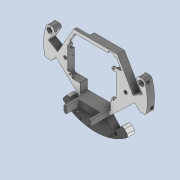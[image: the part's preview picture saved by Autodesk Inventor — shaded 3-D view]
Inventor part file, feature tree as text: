
AUTODESK INVENTOR PART (.ipt)
format: ipt  version: 2020.4 (Build 244396000, 396)  size: 959,488 bytes
history: native  units: mm
features: extrude x28, sketch x28, projected_geometry x14, plane x8, fillet x2
ambient origin geometry x8: Origin, YZ Plane, XZ Plane, XY Plane, X Axis, Y Axis, Z Axis, Center Point
bodies: Solid1 (feature_tree)
feature tree (80):
  extrude  "Extrusion1"  TaperAngle=0.0deg  [1 undecoded]
  extrude  "Extrusion2"  Depth=85.8mm
  extrude  "Extrusion3"  TaperAngle=60.0deg  [1 undecoded]
  extrude  "Extrusion4"  Depth=4.22mm
  extrude  "Extrusion5"  Depth=4.22mm
  extrude  "Extrusion6"  Depth=78.0mm
  extrude  "Extrusion7"  Depth=12.0mm
  extrude  "Extrusion8"  Depth=4.22mm
  fillet  "Fillet1"  Radius=4.22mm
  extrude  "Extrusion9"  Depth=65.0mm
  extrude  "Extrusion10"  TaperAngle=30.0deg  [1 undecoded]
  extrude  "Extrusion11"  TaperAngle=105.0deg  [1 undecoded]
  extrude  "Extrusion12"  Depth=3.0mm
  extrude  "Extrusion13"  Depth=3.0mm
  extrude  "Extrusion14"  Depth=3.0mm
  extrude  "Extrusion15"  Depth=44.0mm
  extrude  "Extrusion16"  Depth=72.0mm
  extrude  "Extrusion17"  Depth=30.0mm
  plane  "Work Plane1"
  extrude  "Extrusion18"  Depth=20.0mm
  plane  "Work Plane2"
  extrude  "Extrusion19"  Depth=3.0mm
  plane  "Work Plane3"
  extrude  "Extrusion20"  Depth=50.0mm
  plane  "Work Plane4"
  extrude  "Extrusion21"  Depth=75.0mm
  plane  "Work Plane5"
  extrude  "Extrusion22"  Depth=25.0mm
  plane  "Work Plane6"
  extrude  "Extrusion23"  Depth=10.0mm
  fillet  "Fillet3"  Radius=10.0mm
  extrude  "Extrusion30"  Depth=5.5mm
  extrude  "Extrusion31"  Depth=5.5mm
  extrude  "Extrusion32"  Depth=3.11mm
  plane  "Work Plane10"
  extrude  "Extrusion33"  Depth=3.11mm
  plane  "Work Plane11"
  extrude  "Extrusion34"  Depth=10.0mm TaperAngle=0.0deg
  sketch  "Sketch1"  dims[d0=171.6mm d1=3.0mm d2=3.0mm d3=3.0mm d4=76.0mm d5=22.0mm d6=73.0mm d7=33.2mm d8=72.0mm d9=32.0mm d10=29.0mm d11=30.0deg d12=150.0deg d13=45.0deg d14=135.0deg d15=18.0mm d16=66.0mm d17=62.0mm d18=60.0mm d19=5.0mm d20=62.240108mm d21=18.0mm d22=66.0mm d23=25.833623mm d24=52.933108mm d25=43.5mm d26=20.0mm d27=66.5mm d28=18.0mm d29=18.0mm d30=0.0mm d31=0.0mm]
  sketch  "Sketch3"  dims[d32=12.0mm d33=0.0mm d34=85.8mm]
  sketch  "Sketch4"  dims[d35=60.0deg d36=60.0deg]
  sketch  "Sketch5"  dims[d37=4.22mm d38=4.22mm]
  sketch  "Sketch6"  dims[d39=4.22mm d40=4.22mm]
  sketch  "Sketch7"  dims[d41=9.55mm d42=0.0mm d43=78.0mm]
  sketch  "Sketch8"  dims[d44=78.0mm d45=12.0mm]
  sketch  "Sketch9"  dims[d46=12.0mm d47=4.22mm d48=4.22mm]
  projected_geometry  "Projected Loop1"
  sketch  "Sketch10"  dims[d49=8.0mm d50=0.0mm d51=65.0mm]
  sketch  "Sketch11"  dims[d52=75.0deg d53=30.0deg]
  sketch  "Sketch12"  dims[d54=75.0deg d55=105.0deg]
  projected_geometry  "Projected Loop2"
  sketch  "Sketch13"  dims[d56=3.0mm d57=3.0mm]
  projected_geometry  "Projected Loop3"
  sketch  "Sketch14"  dims[d58=3.0mm d59=3.0mm]
  projected_geometry  "Projected Loop4"
  sketch  "Sketch16"  dims[d60=3.0mm d61=3.0mm]
  projected_geometry  "Projected Loop5"
  sketch  "Sketch17"  dims[d62=44.0mm d63=44.0mm]
  projected_geometry  "Projected Loop6"
  sketch  "Sketch18"  dims[d64=72.0mm d65=72.0mm]
  projected_geometry  "Projected Loop7"
  sketch  "Sketch19"  dims[d66=20.0mm d67=30.0mm]
  projected_geometry  "Projected Loop8"
  sketch  "Sketch20"  dims[d68=30.0mm d69=20.0mm]
  sketch  "Sketch21"  dims[d70=3.0mm d71=3.0mm]
  sketch  "Sketch22"  dims[d72=50.0mm d73=50.0mm]
  projected_geometry  "Projected Loop9"
  sketch  "Sketch23"  dims[d74=75.0mm d75=75.0mm]
  projected_geometry  "Projected Loop10"
  sketch  "Sketch24"  dims[d76=25.0mm d77=25.0mm]
  projected_geometry  "Projected Loop11"
  sketch  "Sketch25"  dims[d78=79.0mm d79=79.0mm d80=10.0mm d81=0.0mm]
  projected_geometry  "Projected Loop12"
  sketch  "Sketch32"  dims[d82=5.5mm d83=5.5mm]
  sketch  "Sketch33"  dims[d84=5.5mm d85=5.5mm]
  projected_geometry  "Projected Loop16"
  sketch  "Sketch34"  dims[d86=2.0mm d87=0.0mm d88=3.11mm]
  projected_geometry  "Projected Loop17"
  sketch  "Sketch35"  dims[d89=3.11mm d90=3.11mm]
  sketch  "Sketch37"  dims[d91=3.11mm d92=4.0mm d93=0.0mm d94=81.0mm d95=53.0mm d96=4.5mm d97=4.5mm d98=10.5mm d99=0.0mm d100=3.7mm d101=5.35mm d102=4.2mm d103=20.5mm d105=0.0mm d106=38.0mm d107=3.0mm d108=6.0mm d109=6.0mm d110=6.0mm d111=6.0mm d112=6.0mm d113=6.0mm d114=6.0mm d115=6.0mm d116=43.5mm d117=0.0mm d118=50.0mm d119=9.0mm d120=3.0mm d121=0.0mm d122=21.5mm d123=10.0mm d124=0.0mm d125=3.0mm d126=1.0mm d127=1.5mm d128=4.0mm d129=45.0mm d130=10.5mm d131=22.5mm d132=30.0mm d133=0.0mm d134=36.0mm d135=10.0mm d136=4.5mm d137=10.0mm d138=0.0mm d139=180.0deg d140=14.0mm d141=7.0mm d142=7.0mm d143=0.0mm d144=3.0mm d145=5.0mm d146=2.436mm d147=12.0mm d148=5.0mm d149=0.0mm d150=0.0mm d151=3.0mm d152=5.0mm d153=2.436mm d154=10.0mm d155=0.0mm d156=3.0mm d157=5.0mm d158=2.436mm d159=10.0mm d160=0.0mm d161=3.0mm d162=5.0mm d163=2.436418mm d164=12.0mm d165=5.0mm d166=0.0mm d167=0.0mm d168=3.0mm d169=3.5mm d170=2.436418mm d171=12.0mm d172=5.0mm d173=0.0mm d174=0.0mm d175=3.0mm d176=3.5mm d177=2.436418mm d178=12.0mm d179=5.0mm d180=0.0mm d181=0.0mm d182=-1.5mm d183=5.5mm d184=3.0mm d185=0.0mm d186=-1.2mm d187=5.5mm d188=3.0mm d189=0.0mm d190=-1.2mm d191=5.5mm d192=3.0mm d193=0.0mm d194=-1.2mm d195=5.5mm d196=3.0mm d197=0.0mm d198=-1.2mm d199=5.5mm d200=3.0mm d201=0.0mm d202=-1.2mm d203=5.5mm d204=3.0mm d205=0.0mm d239=1.0mm d240=3.0mm d241=10.0mm d242=0.0mm d243=6.981317mm d244=6.981317mm d245=20.0mm d247=8.290314mm d249=20.0mm d251=8.290314mm d253=3.0mm d255=2.436418mm d256=5.0mm d257=10.0mm d258=0.0mm d259=3.0mm d260=5.0mm d261=2.436418mm d262=10.0mm d263=0.0mm d264=-2.0mm d265=5.0mm d266=10.0mm d267=0.0mm d268=-2.0mm d269=5.5mm d270=10.0mm d271=0.0mm]
note: 4 required parameter values undecoded (feature->parameter linkage not recoverable at this tier; creation-order binding heuristic only, values carry confidence <= 0.55)
